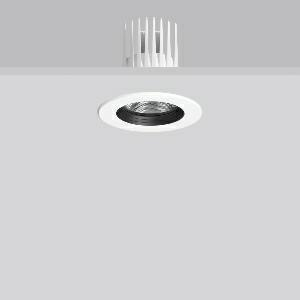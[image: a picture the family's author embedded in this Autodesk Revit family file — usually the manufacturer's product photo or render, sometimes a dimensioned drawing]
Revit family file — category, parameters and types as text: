
# Revit family: heledon_mini_e_901741_002_2_bc10
name_source: partatom
category: Lighting Fixtures
units: mm (PartAtom-declared; Revit-internal decimal feet)

## family parameters
Cut with Voids When Loaded = No
Host = Face
Light Source = No
Part Type = Normal
Room Calculation Point = No
Round Connector Dimension = Use Diameter
Shared = No

## types (1)
- HELEDON mini E (1 x LED Modul 927, 2300 lm, 2700)
    Apparent Load = 20 VA
    Approval mark = CE
    CIE Flux Codes = 99 100 100 100 100
    Color Rendering = 92
    Color Temperature = 2700
    Default Elevation = 1800 mm
    Description = Series: HELEDON mini
Round recessed downlight. Housing: die-cast aluminium, powder-coated. Black plastic ring and recessed LED to prevent glare from the side. Optical assembly with reflector made of MIRO-Silver with 98% total light reflection for outstanding efficiency - can be changed without tools. Best colour rendering index Ra>90. Suitable for Recessed ceiling mounting. Installation without tools thanks to spring fastening system. Including separate LED converter with connecting cable 600 mm.High quality converter without flickering and stroboscopic effect. Through-wiring box (5 pole) available as accessory. The following accessories can be mounted without use of tools: interchangeable lenses, decorative glasses, honeycomb louvre, clear and frosted diffusers, white interchangeable plastic ring. 
Colour: traffic white, matt (RAL 9016)
Diameter: 124 mm
Height: 3 mm
Cut-out diameter: 114 mm
Recess height: 170 mm
Luminaire: recess height: 120 mm
Lamp: LED
Socket: without socket
Colour temperature: 2700K
Colour rendering index (CRI): 92
System power: 20 W
Rated luminous flux: 2300 lm
Luminous efficiency: 115 lm/W
Control gear: Regulated power supply
Protection class: II
Type of protection: IP 20
    Height = 0 mm  [stored 0 ft]
    Lamp = 1 x LED Modul 927
    Lamp Light Flux = 2300 lm
    Lamp count = 1
    Length = 124 mm  [stored 0.406824 ft]
    Lifetime = 50000 h
    Luminous efficacy = 115 lm/W
    Manufacturer = RZB
    ModVariant = No
    Model = 901741.002.2
    Mounting Place = Ceiling
    Mounting Type = Recessed
    Number of Poles = 1
    OnlyDefault = Yes
    Power Factor = 1
    Product Name = HELEDON mini E
    Product group = Recessed downlights
    ProductGroupID = 402
    Protection Class = Protection class II
    Protection Degree = IP 20
    RLX_Detail_Level = 1
    RLX_Emergency_Light_Flux = 0 lm
    RLX_Emergency_Type = 0
    RLX_Emergency_Type_DB = No
    RlxData = <blob elided: 126197 chars, md5=b355c9b7>
    Socket = socket
    Standby Power = 0 W
    System Light Flux = 2300 lm
    System Power = 20 W
    Type Comments = Product without accessories
    Type Image = 901657.002.jpg
    URL = http://relux.com
    VarID = ---
    Voltage = 230 V
    Voltage Range = 220-240 V
    Weight = 0.00 kg
    Width = 0 mm  [stored 0 ft]

note: [stored X ft] marks values corroborated as IEEE doubles in the binary element streams (Revit-internal decimal feet)

## geometry (parser evidence)
native form markers: Blend x4, Sweep x11
no freeform markers — native parametric forms only
